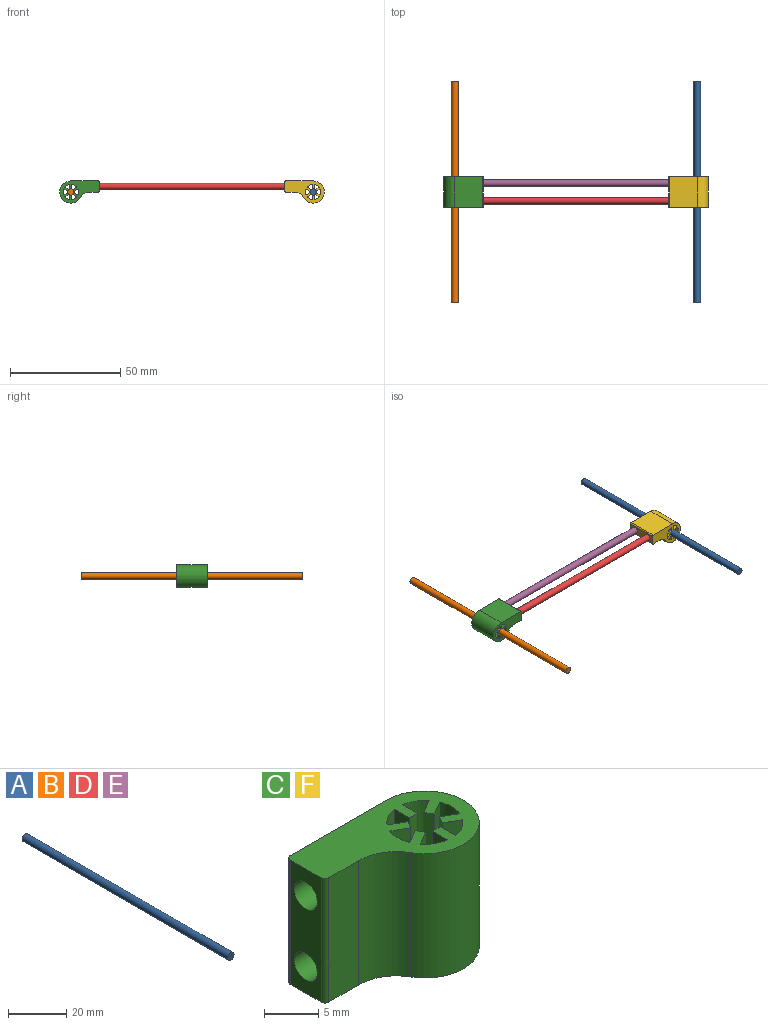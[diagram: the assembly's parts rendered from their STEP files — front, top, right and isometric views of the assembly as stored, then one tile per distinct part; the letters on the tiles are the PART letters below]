
ASSEMBLY  parts=6 mates=5
PART A: 3 faces, bbox 3x100x3 mm
  f0: cylinder r=1.5mm len=100mm, axis (0,1,0), area 942.5mm2, adj f1,f2
  f1: plane 3x3mm, normal (0,-1,0), area 7.1mm2, adj f0
  f2: plane 3x3mm, normal (0,1,0), area 7.1mm2, adj f0
PART B: same geometry as A
PART C: 37 faces, bbox 18x10x14 mm
  f0: cylinder r=5mm len=14mm, axis (0,0,-1), area 293.2mm2, adj f1,f28,f29,f30
  f1: plane 14x12.5mm, normal (0,1,0), area 175mm2, adj f0,f28,f29,f31
  f2: plane 14x4mm, normal (-1,0,0), area 41.9mm2, adj f28,f29,f31,f32,f33,f35
  f3: cylinder r=3.5mm len=14mm, axis (0,0,-1), area 37.3mm2, adj f4,f26,f28,f29
  f4: plane 14x1.96mm, normal (-1,0,0), area 27.5mm2, adj f3,f5,f28,f29
  f5: plane 14x1mm, normal (0,-1,0), area 14mm2, adj f4,f6,f28,f29
  f6: plane 14x1.96mm, normal (1,0,0), area 27.5mm2, adj f5,f7,f28,f29
  f7: cylinder r=3.5mm len=14mm, axis (0,0,-1), area 37.3mm2, adj f6,f8,f28,f29
  f8: plane 14x1.7mm, normal (-0.5,0.87,0), area 27.5mm2, adj f7,f9,f28,f29
  f9: plane 14x0.87mm, normal (-0.87,-0.5,0), area 14mm2, adj f8,f10,f28,f29
  f10: plane 14x1.7mm, normal (0.5,-0.87,0), area 27.5mm2, adj f9,f11,f28,f29
  f11: cylinder r=3.5mm len=14mm, axis (0,0,-1), area 37.3mm2, adj f10,f12,f28,f29
  f12: plane 14x1.7mm, normal (0.5,0.87,0), area 27.5mm2, adj f11,f13,f28,f29
  f13: plane 14x0.87mm, normal (-0.87,0.5,0), area 14mm2, adj f12,f14,f28,f29
  f14: plane 14x1.7mm, normal (-0.5,-0.87,0), area 27.5mm2, adj f13,f15,f28,f29
  f15: cylinder r=3.5mm len=14mm, axis (0,0,-1), area 37.3mm2, adj f14,f16,f28,f29
  f16: plane 14x1.96mm, normal (1,0,0), area 27.5mm2, adj f15,f17,f28,f29
  f17: plane 14x1mm, normal (0,1,0), area 14mm2, adj f16,f18,f28,f29
  f18: plane 14x1.96mm, normal (-1,0,0), area 27.5mm2, adj f17,f19,f28,f29
  f19: cylinder r=3.5mm len=14mm, axis (0,0,-1), area 37.3mm2, adj f18,f20,f28,f29
  f20: plane 14x1.7mm, normal (0.5,-0.87,0), area 27.5mm2, adj f19,f21,f28,f29
  f21: plane 14x0.87mm, normal (0.87,0.5,0), area 14mm2, adj f20,f22,f28,f29
  f22: plane 14x1.7mm, normal (-0.5,0.87,0), area 27.5mm2, adj f21,f23,f28,f29
  f23: cylinder r=3.5mm len=14mm, axis (0,0,-1), area 37.3mm2, adj f22,f24,f28,f29
  f24: plane 14x1.7mm, normal (-0.5,-0.87,0), area 27.5mm2, adj f23,f25,f28,f29
  f25: plane 14x0.87mm, normal (0.87,-0.5,0), area 14mm2, adj f24,f26,f28,f29
  f26: plane 14x1.7mm, normal (0.5,0.87,0), area 27.5mm2, adj f3,f25,f28,f29
  f27: plane 14x3.84mm, normal (0,-1,0), area 53.8mm2, adj f28,f29,f30,f32
  f28: plane 18x10mm, normal (0,0,1), area 99.3mm2, adj f0,f1,f2,f3,f4,f5,f6,f7
  f29: plane 18x10mm, normal (0,0,-1), area 99.3mm2, adj f0,f1,f2,f3,f4,f5,f6,f7
  f30: cylinder r=5mm len=14mm, axis (0,0,-1), area 73.3mm2, adj f0,f27,f28,f29
  f31: cylinder r=0.5mm len=14mm, axis (0,0,-1), area 11mm2, adj f1,f2,f28,f29
  f32: cylinder r=0.5mm len=14mm, axis (0,0,-1), area 11mm2, adj f2,f27,f28,f29
  f33: cylinder r=1.5mm len=8mm, axis (-1,0,0), area 75.4mm2, adj f2,f34
  f34: plane 3x3mm, normal (-1,0,0), area 7.1mm2, adj f33
  f35: cylinder r=1.5mm len=8mm, axis (-1,0,0), area 75.4mm2, adj f2,f36
  f36: plane 3x3mm, normal (-1,0,0), area 7.1mm2, adj f35
PART D: same geometry as A
PART E: same geometry as A
PART F: same geometry as C
PLACE A t=(-0.01,-5.56,0)mm fixed
PLACE B rot(axis=(1,0,0),0deg) t=(-110.01,-5.56,0)mm fixed
PLACE C rot(axis=(0,0.71,0.71),180deg) t=(-110.01,-5.56,0)mm
PLACE D rot(axis=(-0.71,0.71,0),180deg) t=(-55.01,-9.56,2.5)mm
PLACE E rot(axis=(-0.71,0.71,0),180deg) t=(-55.01,-1.56,2.5)mm
PLACE F rot(axis=(1,0,0),90deg) t=(-0.01,-5.56,0)mm
MATE fastened E.f0 <-> F.f33  axis (1,0,0) through (-5.01,-1.56,2.5)mm
MATE fastened D.f0 <-> C.f33  axis (-1,0,0) through (-105.01,-9.56,2.5)mm
MATE fastened D.f0 <-> F.f35  axis (1,0,0) through (-5.01,-9.56,2.5)mm
MATE slider A.f0 <-> F.f7  axis (0,1,0) through (-0.01,-5.56,0)mm
MATE slider B.f0 <-> C.f7  axis (0,1,0) through (-110.01,-5.56,0)mm
